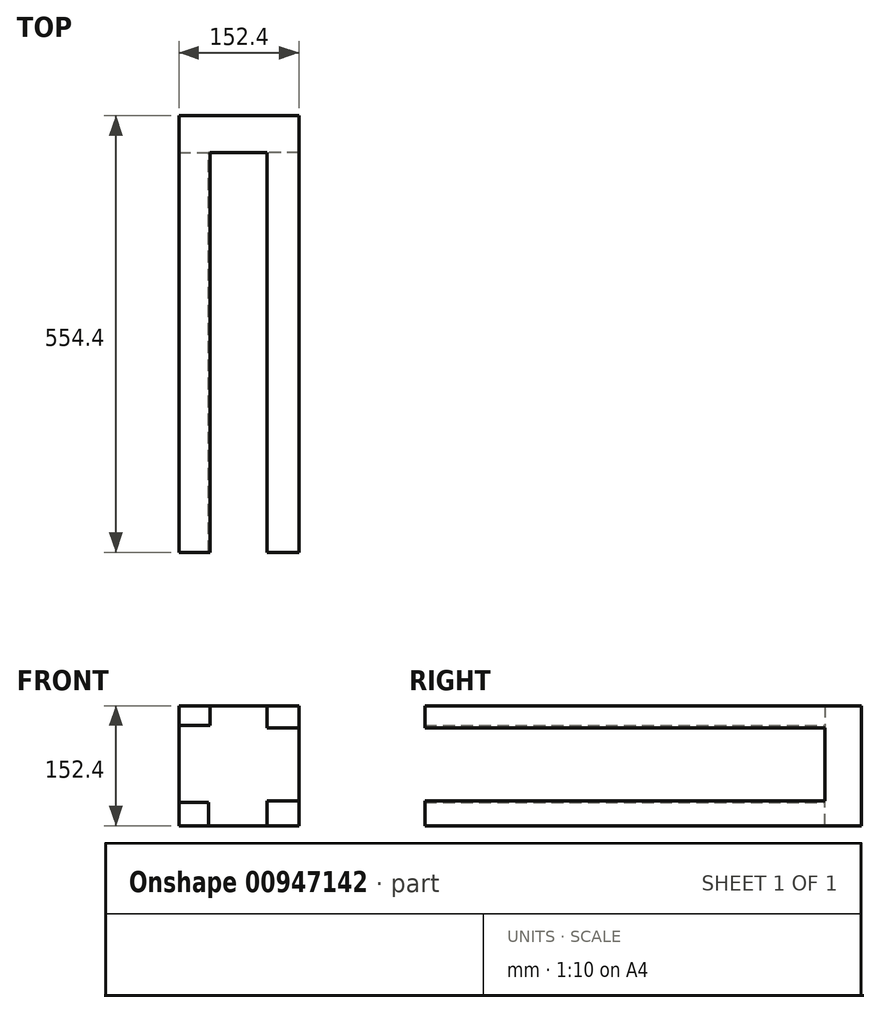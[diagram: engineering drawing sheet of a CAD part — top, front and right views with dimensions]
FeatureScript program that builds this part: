
annotation { "Feature Type Name" : "Feature", "Feature Type Description" : "" }
export const myFeature = defineFeature(function(context is Context, id is Id, definition is map)
    precondition{}
    {
        {
            var Q0;
            Q0=qCreatedBy(makeId("Front.planeOp"),FACE);
            var sketch = newSketch(context, id + "F0", { "sketchPlane" : qUnion([Q0])});
            skLineSegment(sketch, "E0.bottom", {"start": v(76.2, -76.2) * mm, "end": v(-76.2, -76.2) * mm});
            skLineSegment(sketch, "E0.top", {"start": v(76.2, 76.2) * mm, "end": v(-76.2, 76.2) * mm});
            skLineSegment(sketch, "E0.left", {"start": v(76.2, -76.2) * mm, "end": v(76.2, 76.2) * mm});
            skLineSegment(sketch, "E0.right", {"start": v(-76.2, -76.2) * mm, "end": v(-76.2, 76.2) * mm});
            skPoint(sketch, "E0.middle", {"position": v(0, 0) * mm});
            skSolve(sketch);
        }
        {
            var Q0;
            Q0 = qSketchRegion(id + "F0", true);
            extrude(context, id + "F1", {"entities" : qUnion([Q0]), "depth" : 46.4 * mm, "offsetDistance" : 25.4 * mm});
        }
        {
            var Q0;
            Q0=makeQuery(id+"F1.opExtrude","CAP_FACE",FACE,{"disambiguationData":[OSD([sQuery(id+"F0.wireOp",EDGE,"E0.bottom"),sQuery(id+"F0.wireOp",EDGE,"E0.top"),sQuery(id+"F0.wireOp",EDGE,"E0.left"),sQuery(id+"F0.wireOp",EDGE,"E0.right")])],"isStart":false});
            var sketch = newSketch(context, id + "F2", { "sketchPlane" : qUnion([Q0])});
            skLineSegment(sketch, "E1.bottom", {"start": v(-76.2, -76.2) * mm, "end": v(-38.35, -76.2) * mm});
            skLineSegment(sketch, "E1.top", {"start": v(-76.2, -46.4) * mm, "end": v(-38.35, -46.4) * mm});
            skLineSegment(sketch, "E1.left", {"start": v(-76.2, -76.2) * mm, "end": v(-76.2, -46.4) * mm});
            skLineSegment(sketch, "E1.right", {"start": v(-38.35, -76.2) * mm, "end": v(-38.35, -46.4) * mm});
            skLineSegment(sketch, "E2", {"start": v(-76.2, 0) * mm, "end": v(76.2, 0) * mm, "construction": true});
            skLineSegment(sketch, "E3.MirrorCS", {"start": v(-38.35, 228.6) * mm, "end": v(-38.35, 198.8) * mm});
            skLineSegment(sketch, "E4.MirrorCS", {"start": v(-76.2, 198.8) * mm, "end": v(-38.35, 198.8) * mm});
            skLineSegment(sketch, "E5.bottom", {"start": v(-76.2, 76.2) * mm, "end": v(-36.69, 76.2) * mm});
            skLineSegment(sketch, "E5.top", {"start": v(-76.2, 51.38) * mm, "end": v(-36.69, 51.38) * mm});
            skLineSegment(sketch, "E5.left", {"start": v(-76.2, 76.2) * mm, "end": v(-76.2, 51.38) * mm});
            skLineSegment(sketch, "E5.right", {"start": v(-36.69, 76.2) * mm, "end": v(-36.69, 51.38) * mm});
            skLineSegment(sketch, "E6.bottom", {"start": v(76.2, -76.2) * mm, "end": v(35.5, -76.2) * mm});
            skLineSegment(sketch, "E6.top", {"start": v(76.2, -44.51) * mm, "end": v(35.5, -44.51) * mm});
            skLineSegment(sketch, "E6.left", {"start": v(76.2, -76.2) * mm, "end": v(76.2, -44.51) * mm});
            skLineSegment(sketch, "E6.right", {"start": v(35.5, -76.2) * mm, "end": v(35.5, -44.51) * mm});
            skLineSegment(sketch, "E7.bottom", {"start": v(76.2, 76.2) * mm, "end": v(35.5, 76.2) * mm});
            skLineSegment(sketch, "E7.top", {"start": v(76.2, 48.18) * mm, "end": v(35.5, 48.18) * mm});
            skLineSegment(sketch, "E7.left", {"start": v(76.2, 76.2) * mm, "end": v(76.2, 48.18) * mm});
            skLineSegment(sketch, "E7.right", {"start": v(35.5, 76.2) * mm, "end": v(35.5, 48.18) * mm});
            skSolve(sketch);
        }
        {
            var Q0;
            Q0 = qSketchRegion(id + "F2", true);
            extrude(context, id + "F3", {"entities" : qUnion([Q0]), "operationType" : NewBodyOperationType.ADD, "depth" : 508 * mm, "offsetDistance" : 25.4 * mm});
        }
    });
